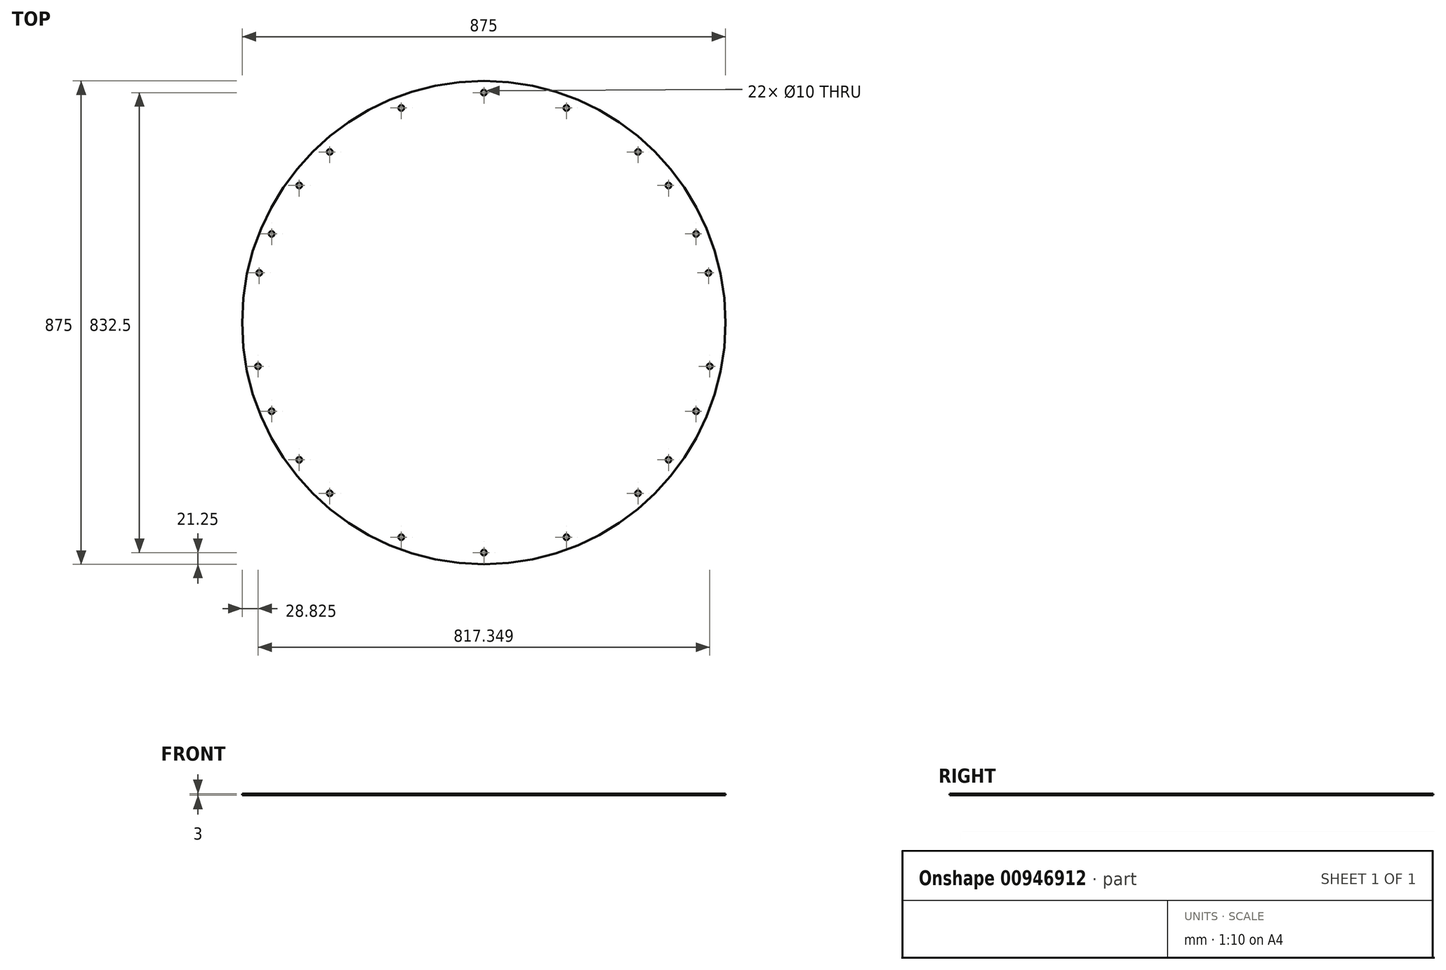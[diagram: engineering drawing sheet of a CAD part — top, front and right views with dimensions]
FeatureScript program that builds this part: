
annotation { "Feature Type Name" : "Feature", "Feature Type Description" : "" }
export const myFeature = defineFeature(function(context is Context, id is Id, definition is map)
    precondition{}
    {
        {
            var Q0;
            Q0=qCreatedBy(makeId("Top.planeOp"),FACE);
            var sketch = newSketch(context, id + "F0", { "sketchPlane" : qUnion([Q0])});
            skCircle(sketch, "E0", {"center": v(0, 0) * mm, "radius": 437.5 * mm});
            skCircle(sketch, "E1", {"center": v(0, 0) * mm, "radius": 395 * mm});
            skCircle(sketch, "E2", {"center": v(0, 0) * mm, "radius": 411.25 * mm});
            skCircle(sketch, "E3", {"center": v(0, 0) * mm, "radius": 421.25 * mm});
            skCircle(sketch, "E4", {"center": v(0, 0) * mm, "radius": 416.25 * mm});
            skCircle(sketch, "E5", {"center": v(0, 416.25) * mm, "radius": 5 * mm});
            skCircle(sketch, "E6", {"center": v(-149.44, 388.5) * mm, "radius": 5 * mm});
            skCircle(sketch, "E7", {"center": v(-278.96, 308.94) * mm, "radius": 5 * mm});
            skCircle(sketch, "E8", {"center": v(-334.11, 248.26) * mm, "radius": 5 * mm});
            skCircle(sketch, "E9", {"center": v(-384.07, 160.48) * mm, "radius": 5 * mm});
            skCircle(sketch, "E10", {"center": v(-406.42, 89.93) * mm, "radius": 5 * mm});
            skCircle(sketch, "E11", {"center": v(-408.67, -79.05) * mm, "radius": 5 * mm});
            skCircle(sketch, "E12", {"center": v(0, -416.25) * mm, "radius": 5 * mm});
            skCircle(sketch, "E13", {"center": v(-149.44, -388.5) * mm, "radius": 5 * mm});
            skCircle(sketch, "E14", {"center": v(149.44, -388.5) * mm, "radius": 5 * mm});
            skCircle(sketch, "E15", {"center": v(-278.96, -308.94) * mm, "radius": 5 * mm});
            skCircle(sketch, "E16", {"center": v(-334.11, -248.26) * mm, "radius": 5 * mm});
            skCircle(sketch, "E17", {"center": v(-384.07, -160.48) * mm, "radius": 5 * mm});
            skCircle(sketch, "E18", {"center": v(149.44, 388.5) * mm, "radius": 5 * mm});
            skCircle(sketch, "E19", {"center": v(278.96, 308.94) * mm, "radius": 5 * mm});
            skCircle(sketch, "E20", {"center": v(334.11, 248.26) * mm, "radius": 5 * mm});
            skCircle(sketch, "E21", {"center": v(384.07, 160.48) * mm, "radius": 5 * mm});
            skCircle(sketch, "E22", {"center": v(406.42, 89.93) * mm, "radius": 5 * mm});
            skCircle(sketch, "E23", {"center": v(408.67, -79.05) * mm, "radius": 5 * mm});
            skCircle(sketch, "E24", {"center": v(278.96, -308.94) * mm, "radius": 5 * mm});
            skCircle(sketch, "E25", {"center": v(334.11, -248.26) * mm, "radius": 5 * mm});
            skCircle(sketch, "E26", {"center": v(384.07, -160.48) * mm, "radius": 5 * mm});
            skSolve(sketch);
        }
        {
            var Q0;
            Q0 = qSketchRegion(id + "F0", true);
            var Q1;
            Q1=makeQuery(id+"F0.imprint","IMPRINT",FACE,{"disambiguationData":[TD([[makeQuery(id+"F0.imprint","IMPRINT",EDGE,{"derivedFrom":sQuery(id+"F0.wireOp",EDGE,"E1")}),1.0]])]});
            var Q2;
            Q2=makeQuery(id+"F0.imprint","IMPRINT",FACE,{"disambiguationData":[TD([[makeQuery(id+"F0.imprint","IMPRINT",EDGE,{"derivedFrom":sQuery(id+"F0.wireOp",EDGE,"E1")}),-1.0]])]});
            var Q3;
            {var subQ0=sQuery(id+"F0.wireOp",EDGE,"E8");var subQ1=sQuery(id+"F0.wireOp",EDGE,"E2");var subQ2=makeQuery(id+"F0.imprint","INTERSECT",VERTEX,{"derivedFrom":[subQ1,subQ0]});Q3=makeQuery(id+"F0.imprint","IMPRINT",FACE,{"disambiguationData":[TD([[makeQuery(id+"F0.imprint","IMPRINT",EDGE,{"disambiguationData":[TD([[subQ2,-1.0]])],"derivedFrom":subQ1}),-1.0]])]});}
            var Q4;
            {var subQ0=sQuery(id+"F0.wireOp",EDGE,"E8");var subQ1=sQuery(id+"F0.wireOp",EDGE,"E3");var subQ2=makeQuery(id+"F0.imprint","INTERSECT",VERTEX,{"derivedFrom":[subQ1,subQ0]});Q4=makeQuery(id+"F0.imprint","IMPRINT",FACE,{"disambiguationData":[TD([[makeQuery(id+"F0.imprint","IMPRINT",EDGE,{"disambiguationData":[TD([[subQ2,-1.0]])],"derivedFrom":subQ1}),1.0]])]});}
            var Q5;
            {var subQ0=sQuery(id+"F0.wireOp",EDGE,"E7");var subQ1=sQuery(id+"F0.wireOp",EDGE,"E2");var subQ2=makeQuery(id+"F0.imprint","INTERSECT",VERTEX,{"derivedFrom":[subQ1,subQ0]});Q5=makeQuery(id+"F0.imprint","IMPRINT",FACE,{"disambiguationData":[TD([[makeQuery(id+"F0.imprint","IMPRINT",EDGE,{"disambiguationData":[TD([[subQ2,-1.0]])],"derivedFrom":subQ1}),-1.0]])]});}
            var Q6;
            {var subQ0=sQuery(id+"F0.wireOp",EDGE,"E7");var subQ1=sQuery(id+"F0.wireOp",EDGE,"E3");var subQ2=makeQuery(id+"F0.imprint","INTERSECT",VERTEX,{"derivedFrom":[subQ1,subQ0]});Q6=makeQuery(id+"F0.imprint","IMPRINT",FACE,{"disambiguationData":[TD([[makeQuery(id+"F0.imprint","IMPRINT",EDGE,{"disambiguationData":[TD([[subQ2,-1.0]])],"derivedFrom":subQ1}),1.0]])]});}
            var Q7;
            {var subQ0=sQuery(id+"F0.wireOp",EDGE,"E6");var subQ1=sQuery(id+"F0.wireOp",EDGE,"E2");var subQ2=makeQuery(id+"F0.imprint","INTERSECT",VERTEX,{"derivedFrom":[subQ1,subQ0]});Q7=makeQuery(id+"F0.imprint","IMPRINT",FACE,{"disambiguationData":[TD([[makeQuery(id+"F0.imprint","IMPRINT",EDGE,{"disambiguationData":[TD([[subQ2,-1.0]])],"derivedFrom":subQ1}),-1.0]])]});}
            var Q8;
            {var subQ0=sQuery(id+"F0.wireOp",EDGE,"E6");var subQ1=sQuery(id+"F0.wireOp",EDGE,"E3");var subQ2=makeQuery(id+"F0.imprint","INTERSECT",VERTEX,{"derivedFrom":[subQ1,subQ0]});Q8=makeQuery(id+"F0.imprint","IMPRINT",FACE,{"disambiguationData":[TD([[makeQuery(id+"F0.imprint","IMPRINT",EDGE,{"disambiguationData":[TD([[subQ2,-1.0]])],"derivedFrom":subQ1}),1.0]])]});}
            var Q9;
            {var subQ0=sQuery(id+"F0.wireOp",EDGE,"E9");var subQ1=sQuery(id+"F0.wireOp",EDGE,"E2");var subQ2=makeQuery(id+"F0.imprint","INTERSECT",VERTEX,{"derivedFrom":[subQ1,subQ0]});Q9=makeQuery(id+"F0.imprint","IMPRINT",FACE,{"disambiguationData":[TD([[makeQuery(id+"F0.imprint","IMPRINT",EDGE,{"disambiguationData":[TD([[subQ2,-1.0]])],"derivedFrom":subQ1}),-1.0]])]});}
            var Q10;
            {var subQ0=sQuery(id+"F0.wireOp",EDGE,"E9");var subQ1=sQuery(id+"F0.wireOp",EDGE,"E3");var subQ2=makeQuery(id+"F0.imprint","INTERSECT",VERTEX,{"derivedFrom":[subQ1,subQ0]});Q10=makeQuery(id+"F0.imprint","IMPRINT",FACE,{"disambiguationData":[TD([[makeQuery(id+"F0.imprint","IMPRINT",EDGE,{"disambiguationData":[TD([[subQ2,-1.0]])],"derivedFrom":subQ1}),1.0]])]});}
            var Q11;
            {var subQ0=sQuery(id+"F0.wireOp",EDGE,"E10");var subQ1=sQuery(id+"F0.wireOp",EDGE,"E2");var subQ2=makeQuery(id+"F0.imprint","INTERSECT",VERTEX,{"derivedFrom":[subQ1,subQ0]});Q11=makeQuery(id+"F0.imprint","IMPRINT",FACE,{"disambiguationData":[TD([[makeQuery(id+"F0.imprint","IMPRINT",EDGE,{"disambiguationData":[TD([[subQ2,-1.0]])],"derivedFrom":subQ1}),-1.0]])]});}
            var Q12;
            {var subQ0=sQuery(id+"F0.wireOp",EDGE,"E10");var subQ1=sQuery(id+"F0.wireOp",EDGE,"E3");var subQ2=makeQuery(id+"F0.imprint","INTERSECT",VERTEX,{"derivedFrom":[subQ1,subQ0]});Q12=makeQuery(id+"F0.imprint","IMPRINT",FACE,{"disambiguationData":[TD([[makeQuery(id+"F0.imprint","IMPRINT",EDGE,{"disambiguationData":[TD([[subQ2,-1.0]])],"derivedFrom":subQ1}),1.0]])]});}
            var Q13;
            {var subQ0=sQuery(id+"F0.wireOp",EDGE,"E5");var subQ1=sQuery(id+"F0.wireOp",EDGE,"E2");var subQ2=makeQuery(id+"F0.imprint","INTERSECT",VERTEX,{"derivedFrom":[subQ1,subQ0]});Q13=makeQuery(id+"F0.imprint","IMPRINT",FACE,{"disambiguationData":[TD([[makeQuery(id+"F0.imprint","IMPRINT",EDGE,{"disambiguationData":[TD([[subQ2,-1.0]])],"derivedFrom":subQ1}),-1.0]])]});}
            var Q14;
            {var subQ0=sQuery(id+"F0.wireOp",EDGE,"E5");var subQ1=sQuery(id+"F0.wireOp",EDGE,"E3");var subQ2=makeQuery(id+"F0.imprint","INTERSECT",VERTEX,{"derivedFrom":[subQ1,subQ0]});Q14=makeQuery(id+"F0.imprint","IMPRINT",FACE,{"disambiguationData":[TD([[makeQuery(id+"F0.imprint","IMPRINT",EDGE,{"disambiguationData":[TD([[subQ2,-1.0]])],"derivedFrom":subQ1}),1.0]])]});}
            var Q15;
            {var subQ0=sQuery(id+"F0.wireOp",EDGE,"E18");var subQ1=sQuery(id+"F0.wireOp",EDGE,"E2");var subQ2=makeQuery(id+"F0.imprint","INTERSECT",VERTEX,{"derivedFrom":[subQ1,subQ0]});Q15=makeQuery(id+"F0.imprint","IMPRINT",FACE,{"disambiguationData":[TD([[makeQuery(id+"F0.imprint","IMPRINT",EDGE,{"disambiguationData":[TD([[subQ2,-1.0]])],"derivedFrom":subQ1}),-1.0]])]});}
            var Q16;
            {var subQ0=sQuery(id+"F0.wireOp",EDGE,"E18");var subQ1=sQuery(id+"F0.wireOp",EDGE,"E3");var subQ2=makeQuery(id+"F0.imprint","INTERSECT",VERTEX,{"derivedFrom":[subQ1,subQ0]});Q16=makeQuery(id+"F0.imprint","IMPRINT",FACE,{"disambiguationData":[TD([[makeQuery(id+"F0.imprint","IMPRINT",EDGE,{"disambiguationData":[TD([[subQ2,-1.0]])],"derivedFrom":subQ1}),1.0]])]});}
            var Q17;
            {var subQ0=sQuery(id+"F0.wireOp",EDGE,"E19");var subQ1=sQuery(id+"F0.wireOp",EDGE,"E2");var subQ2=makeQuery(id+"F0.imprint","INTERSECT",VERTEX,{"derivedFrom":[subQ1,subQ0]});Q17=makeQuery(id+"F0.imprint","IMPRINT",FACE,{"disambiguationData":[TD([[makeQuery(id+"F0.imprint","IMPRINT",EDGE,{"disambiguationData":[TD([[subQ2,-1.0]])],"derivedFrom":subQ1}),-1.0]])]});}
            var Q18;
            {var subQ0=sQuery(id+"F0.wireOp",EDGE,"E19");var subQ1=sQuery(id+"F0.wireOp",EDGE,"E3");var subQ2=makeQuery(id+"F0.imprint","INTERSECT",VERTEX,{"derivedFrom":[subQ1,subQ0]});Q18=makeQuery(id+"F0.imprint","IMPRINT",FACE,{"disambiguationData":[TD([[makeQuery(id+"F0.imprint","IMPRINT",EDGE,{"disambiguationData":[TD([[subQ2,-1.0]])],"derivedFrom":subQ1}),1.0]])]});}
            var Q19;
            {var subQ0=sQuery(id+"F0.wireOp",EDGE,"E20");var subQ1=sQuery(id+"F0.wireOp",EDGE,"E2");var subQ2=makeQuery(id+"F0.imprint","INTERSECT",VERTEX,{"derivedFrom":[subQ1,subQ0]});Q19=makeQuery(id+"F0.imprint","IMPRINT",FACE,{"disambiguationData":[TD([[makeQuery(id+"F0.imprint","IMPRINT",EDGE,{"disambiguationData":[TD([[subQ2,-1.0]])],"derivedFrom":subQ1}),-1.0]])]});}
            var Q20;
            {var subQ0=sQuery(id+"F0.wireOp",EDGE,"E20");var subQ1=sQuery(id+"F0.wireOp",EDGE,"E3");var subQ2=makeQuery(id+"F0.imprint","INTERSECT",VERTEX,{"derivedFrom":[subQ1,subQ0]});Q20=makeQuery(id+"F0.imprint","IMPRINT",FACE,{"disambiguationData":[TD([[makeQuery(id+"F0.imprint","IMPRINT",EDGE,{"disambiguationData":[TD([[subQ2,-1.0]])],"derivedFrom":subQ1}),1.0]])]});}
            var Q21;
            {var subQ0=sQuery(id+"F0.wireOp",EDGE,"E21");var subQ1=sQuery(id+"F0.wireOp",EDGE,"E2");var subQ2=makeQuery(id+"F0.imprint","INTERSECT",VERTEX,{"derivedFrom":[subQ1,subQ0]});Q21=makeQuery(id+"F0.imprint","IMPRINT",FACE,{"disambiguationData":[TD([[makeQuery(id+"F0.imprint","IMPRINT",EDGE,{"disambiguationData":[TD([[subQ2,-1.0]])],"derivedFrom":subQ1}),-1.0]])]});}
            var Q22;
            {var subQ0=sQuery(id+"F0.wireOp",EDGE,"E21");var subQ1=sQuery(id+"F0.wireOp",EDGE,"E3");var subQ2=makeQuery(id+"F0.imprint","INTERSECT",VERTEX,{"derivedFrom":[subQ1,subQ0]});Q22=makeQuery(id+"F0.imprint","IMPRINT",FACE,{"disambiguationData":[TD([[makeQuery(id+"F0.imprint","IMPRINT",EDGE,{"disambiguationData":[TD([[subQ2,-1.0]])],"derivedFrom":subQ1}),1.0]])]});}
            var Q23;
            {var subQ0=sQuery(id+"F0.wireOp",EDGE,"E21");var subQ1=sQuery(id+"F0.wireOp",EDGE,"E2");var subQ2=makeQuery(id+"F0.imprint","INTERSECT",VERTEX,{"derivedFrom":[subQ1,subQ0]});Q23=makeQuery(id+"F0.imprint","IMPRINT",FACE,{"disambiguationData":[TD([[makeQuery(id+"F0.imprint","IMPRINT",EDGE,{"disambiguationData":[TD([[subQ2,1.0]])],"derivedFrom":subQ1}),-1.0]])]});}
            var Q24;
            {var subQ0=sQuery(id+"F0.wireOp",EDGE,"E21");var subQ1=sQuery(id+"F0.wireOp",EDGE,"E3");var subQ2=makeQuery(id+"F0.imprint","INTERSECT",VERTEX,{"derivedFrom":[subQ1,subQ0]});Q24=makeQuery(id+"F0.imprint","IMPRINT",FACE,{"disambiguationData":[TD([[makeQuery(id+"F0.imprint","IMPRINT",EDGE,{"disambiguationData":[TD([[subQ2,1.0]])],"derivedFrom":subQ1}),1.0]])]});}
            var Q25;
            {var subQ0=sQuery(id+"F0.wireOp",EDGE,"E22");var subQ1=sQuery(id+"F0.wireOp",EDGE,"E2");var subQ2=makeQuery(id+"F0.imprint","INTERSECT",VERTEX,{"derivedFrom":[subQ1,subQ0]});Q25=makeQuery(id+"F0.imprint","IMPRINT",FACE,{"disambiguationData":[TD([[makeQuery(id+"F0.imprint","IMPRINT",EDGE,{"disambiguationData":[TD([[subQ2,1.0]])],"derivedFrom":subQ1}),-1.0]])]});}
            var Q26;
            {var subQ0=sQuery(id+"F0.wireOp",EDGE,"E22");var subQ1=sQuery(id+"F0.wireOp",EDGE,"E3");var subQ2=makeQuery(id+"F0.imprint","INTERSECT",VERTEX,{"derivedFrom":[subQ1,subQ0]});Q26=makeQuery(id+"F0.imprint","IMPRINT",FACE,{"disambiguationData":[TD([[makeQuery(id+"F0.imprint","IMPRINT",EDGE,{"disambiguationData":[TD([[subQ2,1.0]])],"derivedFrom":subQ1}),1.0]])]});}
            var Q27;
            {var subQ0=sQuery(id+"F0.wireOp",EDGE,"E26");var subQ1=sQuery(id+"F0.wireOp",EDGE,"E2");var subQ2=makeQuery(id+"F0.imprint","INTERSECT",VERTEX,{"derivedFrom":[subQ1,subQ0]});Q27=makeQuery(id+"F0.imprint","IMPRINT",FACE,{"disambiguationData":[TD([[makeQuery(id+"F0.imprint","IMPRINT",EDGE,{"disambiguationData":[TD([[subQ2,-1.0]])],"derivedFrom":subQ1}),-1.0]])]});}
            var Q28;
            {var subQ0=sQuery(id+"F0.wireOp",EDGE,"E26");var subQ1=sQuery(id+"F0.wireOp",EDGE,"E3");var subQ2=makeQuery(id+"F0.imprint","INTERSECT",VERTEX,{"derivedFrom":[subQ1,subQ0]});Q28=makeQuery(id+"F0.imprint","IMPRINT",FACE,{"disambiguationData":[TD([[makeQuery(id+"F0.imprint","IMPRINT",EDGE,{"disambiguationData":[TD([[subQ2,-1.0]])],"derivedFrom":subQ1}),1.0]])]});}
            var Q29;
            {var subQ0=sQuery(id+"F0.wireOp",EDGE,"E25");var subQ1=sQuery(id+"F0.wireOp",EDGE,"E2");var subQ2=makeQuery(id+"F0.imprint","INTERSECT",VERTEX,{"derivedFrom":[subQ1,subQ0]});Q29=makeQuery(id+"F0.imprint","IMPRINT",FACE,{"disambiguationData":[TD([[makeQuery(id+"F0.imprint","IMPRINT",EDGE,{"disambiguationData":[TD([[subQ2,-1.0]])],"derivedFrom":subQ1}),-1.0]])]});}
            var Q30;
            {var subQ0=sQuery(id+"F0.wireOp",EDGE,"E25");var subQ1=sQuery(id+"F0.wireOp",EDGE,"E3");var subQ2=makeQuery(id+"F0.imprint","INTERSECT",VERTEX,{"derivedFrom":[subQ1,subQ0]});Q30=makeQuery(id+"F0.imprint","IMPRINT",FACE,{"disambiguationData":[TD([[makeQuery(id+"F0.imprint","IMPRINT",EDGE,{"disambiguationData":[TD([[subQ2,-1.0]])],"derivedFrom":subQ1}),1.0]])]});}
            var Q31;
            {var subQ0=sQuery(id+"F0.wireOp",EDGE,"E24");var subQ1=sQuery(id+"F0.wireOp",EDGE,"E2");var subQ2=makeQuery(id+"F0.imprint","INTERSECT",VERTEX,{"derivedFrom":[subQ1,subQ0]});Q31=makeQuery(id+"F0.imprint","IMPRINT",FACE,{"disambiguationData":[TD([[makeQuery(id+"F0.imprint","IMPRINT",EDGE,{"disambiguationData":[TD([[subQ2,-1.0]])],"derivedFrom":subQ1}),-1.0]])]});}
            var Q32;
            {var subQ0=sQuery(id+"F0.wireOp",EDGE,"E24");var subQ1=sQuery(id+"F0.wireOp",EDGE,"E3");var subQ2=makeQuery(id+"F0.imprint","INTERSECT",VERTEX,{"derivedFrom":[subQ1,subQ0]});Q32=makeQuery(id+"F0.imprint","IMPRINT",FACE,{"disambiguationData":[TD([[makeQuery(id+"F0.imprint","IMPRINT",EDGE,{"disambiguationData":[TD([[subQ2,-1.0]])],"derivedFrom":subQ1}),1.0]])]});}
            var Q33;
            {var subQ0=sQuery(id+"F0.wireOp",EDGE,"E11");var subQ1=sQuery(id+"F0.wireOp",EDGE,"E2");var subQ2=makeQuery(id+"F0.imprint","INTERSECT",VERTEX,{"derivedFrom":[subQ1,subQ0]});Q33=makeQuery(id+"F0.imprint","IMPRINT",FACE,{"disambiguationData":[TD([[makeQuery(id+"F0.imprint","IMPRINT",EDGE,{"disambiguationData":[TD([[subQ2,-1.0]])],"derivedFrom":subQ1}),-1.0]])]});}
            var Q34;
            {var subQ0=sQuery(id+"F0.wireOp",EDGE,"E11");var subQ1=sQuery(id+"F0.wireOp",EDGE,"E3");var subQ2=makeQuery(id+"F0.imprint","INTERSECT",VERTEX,{"derivedFrom":[subQ1,subQ0]});Q34=makeQuery(id+"F0.imprint","IMPRINT",FACE,{"disambiguationData":[TD([[makeQuery(id+"F0.imprint","IMPRINT",EDGE,{"disambiguationData":[TD([[subQ2,-1.0]])],"derivedFrom":subQ1}),1.0]])]});}
            var Q35;
            {var subQ0=sQuery(id+"F0.wireOp",EDGE,"E17");var subQ1=sQuery(id+"F0.wireOp",EDGE,"E3");var subQ2=makeQuery(id+"F0.imprint","INTERSECT",VERTEX,{"derivedFrom":[subQ1,subQ0]});Q35=makeQuery(id+"F0.imprint","IMPRINT",FACE,{"disambiguationData":[TD([[makeQuery(id+"F0.imprint","IMPRINT",EDGE,{"disambiguationData":[TD([[subQ2,-1.0]])],"derivedFrom":subQ1}),1.0]])]});}
            var Q36;
            {var subQ0=sQuery(id+"F0.wireOp",EDGE,"E17");var subQ1=sQuery(id+"F0.wireOp",EDGE,"E2");var subQ2=makeQuery(id+"F0.imprint","INTERSECT",VERTEX,{"derivedFrom":[subQ1,subQ0]});Q36=makeQuery(id+"F0.imprint","IMPRINT",FACE,{"disambiguationData":[TD([[makeQuery(id+"F0.imprint","IMPRINT",EDGE,{"disambiguationData":[TD([[subQ2,-1.0]])],"derivedFrom":subQ1}),-1.0]])]});}
            var Q37;
            {var subQ0=sQuery(id+"F0.wireOp",EDGE,"E16");var subQ1=sQuery(id+"F0.wireOp",EDGE,"E3");var subQ2=makeQuery(id+"F0.imprint","INTERSECT",VERTEX,{"derivedFrom":[subQ1,subQ0]});Q37=makeQuery(id+"F0.imprint","IMPRINT",FACE,{"disambiguationData":[TD([[makeQuery(id+"F0.imprint","IMPRINT",EDGE,{"disambiguationData":[TD([[subQ2,-1.0]])],"derivedFrom":subQ1}),1.0]])]});}
            var Q38;
            {var subQ0=sQuery(id+"F0.wireOp",EDGE,"E16");var subQ1=sQuery(id+"F0.wireOp",EDGE,"E2");var subQ2=makeQuery(id+"F0.imprint","INTERSECT",VERTEX,{"derivedFrom":[subQ1,subQ0]});Q38=makeQuery(id+"F0.imprint","IMPRINT",FACE,{"disambiguationData":[TD([[makeQuery(id+"F0.imprint","IMPRINT",EDGE,{"disambiguationData":[TD([[subQ2,-1.0]])],"derivedFrom":subQ1}),-1.0]])]});}
            var Q39;
            {var subQ0=sQuery(id+"F0.wireOp",EDGE,"E15");var subQ1=sQuery(id+"F0.wireOp",EDGE,"E3");var subQ2=makeQuery(id+"F0.imprint","INTERSECT",VERTEX,{"derivedFrom":[subQ1,subQ0]});Q39=makeQuery(id+"F0.imprint","IMPRINT",FACE,{"disambiguationData":[TD([[makeQuery(id+"F0.imprint","IMPRINT",EDGE,{"disambiguationData":[TD([[subQ2,-1.0]])],"derivedFrom":subQ1}),1.0]])]});}
            var Q40;
            {var subQ0=sQuery(id+"F0.wireOp",EDGE,"E15");var subQ1=sQuery(id+"F0.wireOp",EDGE,"E2");var subQ2=makeQuery(id+"F0.imprint","INTERSECT",VERTEX,{"derivedFrom":[subQ1,subQ0]});Q40=makeQuery(id+"F0.imprint","IMPRINT",FACE,{"disambiguationData":[TD([[makeQuery(id+"F0.imprint","IMPRINT",EDGE,{"disambiguationData":[TD([[subQ2,-1.0]])],"derivedFrom":subQ1}),-1.0]])]});}
            var Q41;
            {var subQ0=sQuery(id+"F0.wireOp",EDGE,"E13");var subQ1=sQuery(id+"F0.wireOp",EDGE,"E3");var subQ2=makeQuery(id+"F0.imprint","INTERSECT",VERTEX,{"derivedFrom":[subQ1,subQ0]});Q41=makeQuery(id+"F0.imprint","IMPRINT",FACE,{"disambiguationData":[TD([[makeQuery(id+"F0.imprint","IMPRINT",EDGE,{"disambiguationData":[TD([[subQ2,-1.0]])],"derivedFrom":subQ1}),1.0]])]});}
            var Q42;
            {var subQ0=sQuery(id+"F0.wireOp",EDGE,"E13");var subQ1=sQuery(id+"F0.wireOp",EDGE,"E2");var subQ2=makeQuery(id+"F0.imprint","INTERSECT",VERTEX,{"derivedFrom":[subQ1,subQ0]});Q42=makeQuery(id+"F0.imprint","IMPRINT",FACE,{"disambiguationData":[TD([[makeQuery(id+"F0.imprint","IMPRINT",EDGE,{"disambiguationData":[TD([[subQ2,-1.0]])],"derivedFrom":subQ1}),-1.0]])]});}
            var Q43;
            {var subQ0=sQuery(id+"F0.wireOp",EDGE,"E12");var subQ1=sQuery(id+"F0.wireOp",EDGE,"E3");var subQ2=makeQuery(id+"F0.imprint","INTERSECT",VERTEX,{"derivedFrom":[subQ1,subQ0]});Q43=makeQuery(id+"F0.imprint","IMPRINT",FACE,{"disambiguationData":[TD([[makeQuery(id+"F0.imprint","IMPRINT",EDGE,{"disambiguationData":[TD([[subQ2,-1.0]])],"derivedFrom":subQ1}),1.0]])]});}
            var Q44;
            {var subQ0=sQuery(id+"F0.wireOp",EDGE,"E12");var subQ1=sQuery(id+"F0.wireOp",EDGE,"E2");var subQ2=makeQuery(id+"F0.imprint","INTERSECT",VERTEX,{"derivedFrom":[subQ1,subQ0]});Q44=makeQuery(id+"F0.imprint","IMPRINT",FACE,{"disambiguationData":[TD([[makeQuery(id+"F0.imprint","IMPRINT",EDGE,{"disambiguationData":[TD([[subQ2,-1.0]])],"derivedFrom":subQ1}),-1.0]])]});}
            var Q45;
            {var subQ0=sQuery(id+"F0.wireOp",EDGE,"E14");var subQ1=sQuery(id+"F0.wireOp",EDGE,"E3");var subQ2=makeQuery(id+"F0.imprint","INTERSECT",VERTEX,{"derivedFrom":[subQ1,subQ0]});Q45=makeQuery(id+"F0.imprint","IMPRINT",FACE,{"disambiguationData":[TD([[makeQuery(id+"F0.imprint","IMPRINT",EDGE,{"disambiguationData":[TD([[subQ2,-1.0]])],"derivedFrom":subQ1}),1.0]])]});}
            var Q46;
            {var subQ0=sQuery(id+"F0.wireOp",EDGE,"E14");var subQ1=sQuery(id+"F0.wireOp",EDGE,"E2");var subQ2=makeQuery(id+"F0.imprint","INTERSECT",VERTEX,{"derivedFrom":[subQ1,subQ0]});Q46=makeQuery(id+"F0.imprint","IMPRINT",FACE,{"disambiguationData":[TD([[makeQuery(id+"F0.imprint","IMPRINT",EDGE,{"disambiguationData":[TD([[subQ2,-1.0]])],"derivedFrom":subQ1}),-1.0]])]});}
            extrude(context, id + "F1", {"entities" : qUnion([Q0, Q1, Q2, Q3, Q4, Q5, Q6, Q7, Q8, Q9, Q10, Q11, Q12, Q13, Q14, Q15, Q16, Q17, Q18, Q19, Q20, Q21, Q22, Q23, Q24, Q25, Q26, Q27, Q28, Q29, Q30, Q31, Q32, Q33, Q34, Q35, Q36, Q37, Q38, Q39, Q40, Q41, Q42, Q43, Q44, Q45, Q46]), "depth" : 3 * mm, "offsetDistance" : 25 * mm});
        }
    });
